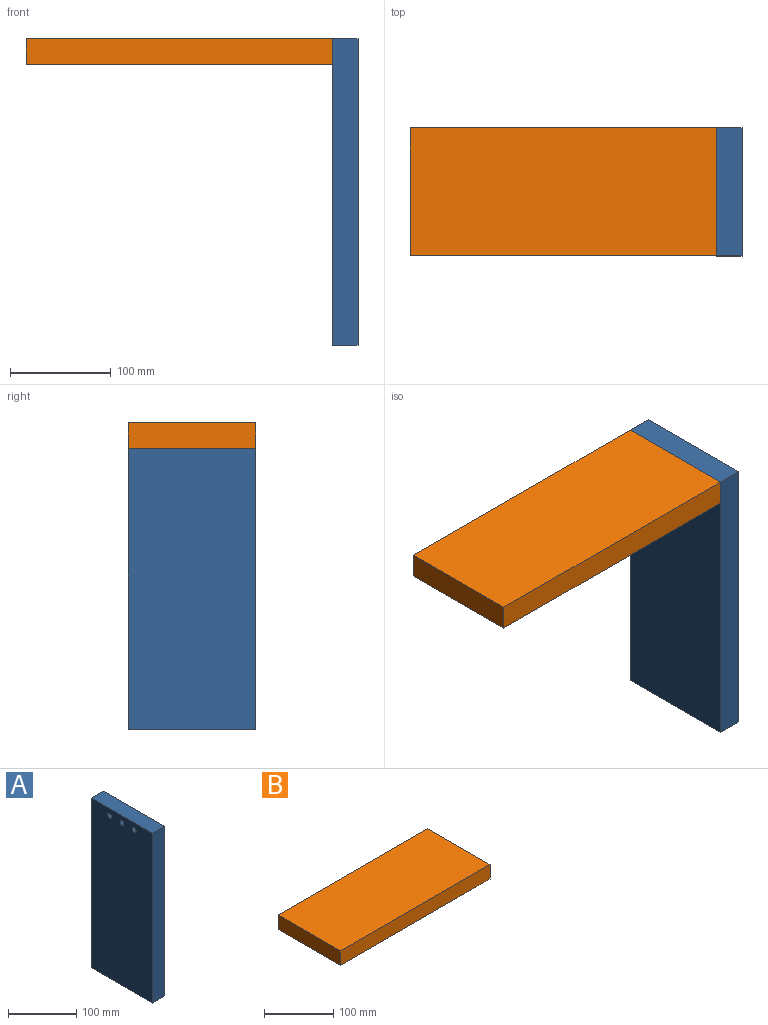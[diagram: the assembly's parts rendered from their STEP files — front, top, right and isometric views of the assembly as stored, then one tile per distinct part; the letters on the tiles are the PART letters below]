
ASSEMBLY  parts=2 mates=1
PART A: 14 faces, bbox 25.4x127x304.8 mm
  f0: plane 304.8x25.4mm, normal (0,1,0), area 7741.9mm2, adj f1,f3,f4,f5
  f1: plane 127x25.4mm, normal (0,0,1), area 3225.8mm2, adj f0,f2,f4,f5
  f2: plane 304.8x25.4mm, normal (0,-1,0), area 7741.9mm2, adj f1,f3,f4,f5
  f3: plane 127x25.4mm, normal (0,0,-1), area 3225.8mm2, adj f0,f2,f4,f5
  f4: plane 304.8x127mm, normal (1,0,0), area 38709.6mm2, adj f0,f1,f2,f3
  f5: plane 304.8x127mm, normal (-1,0,0), area 38558.8mm2, adj f0,f1,f2,f3,f6,f9,f12
  f6: cylinder r=4mm len=12.7mm, axis (-1,0,0), area 319.2mm2, adj f5,f8
  f7: plane 4.83x4.83mm, normal (-1,0,0), area 18.3mm2, adj f8
  f8: cone r=4mm half-angle=45deg, axis (-1,0,0), area 45.2mm2, adj f6,f7
  f9: cylinder r=4mm len=12.7mm, axis (-1,0,0), area 319.2mm2, adj f5,f11
  f10: plane 4.83x4.83mm, normal (-1,0,0), area 18.3mm2, adj f11
  f11: cone r=4mm half-angle=45deg, axis (-1,0,0), area 45.2mm2, adj f9,f10
  f12: cylinder r=4mm len=10.32mm, axis (-1,0,0), area 259.4mm2, adj f5,f13
  f13: plane 8x8mm, normal (-1,0,0), area 50.3mm2, adj f12
PART B: 14 faces, bbox 304.8x127x25.4 mm
  f0: plane 127x25.4mm, normal (1,0,0), area 3075mm2, adj f1,f3,f4,f5,f6,f9,f12
  f1: plane 304.8x25.4mm, normal (0,1,0), area 7741.9mm2, adj f0,f2,f4,f5
  f2: plane 127x25.4mm, normal (-1,0,0), area 3225.8mm2, adj f1,f3,f4,f5
  f3: plane 304.8x25.4mm, normal (0,-1,0), area 7741.9mm2, adj f0,f2,f4,f5
  f4: plane 304.8x127mm, normal (0,0,1), area 38709.6mm2, adj f0,f1,f2,f3
  f5: plane 304.8x127mm, normal (0,0,-1), area 38709.6mm2, adj f0,f1,f2,f3
  f6: cylinder r=4mm len=25.4mm, axis (1,0,0), area 638.4mm2, adj f0,f8
  f7: plane 4.83x4.83mm, normal (1,0,0), area 18.3mm2, adj f8
  f8: cone r=4mm half-angle=45deg, axis (1,0,0), area 45.2mm2, adj f6,f7
  f9: cylinder r=4mm len=25.4mm, axis (1,0,0), area 638.4mm2, adj f0,f11
  f10: plane 4.83x4.83mm, normal (1,0,0), area 18.3mm2, adj f11
  f11: cone r=4mm half-angle=45deg, axis (1,0,0), area 45.2mm2, adj f9,f10
  f12: cylinder r=4mm len=10.32mm, axis (-1,0,0), area 259.4mm2, adj f0,f13
  f13: plane 8x8mm, normal (1,0,0), area 50.3mm2, adj f12
PLACE A t=(-155.73,-121.65,-47.6)mm
PLACE B t=(-155.73,-121.65,-47.6)mm fixed
MATE fastened B.f11 <-> A.f8  axis (1,0,0) through (-3.33,-147.05,-34.9)mm
